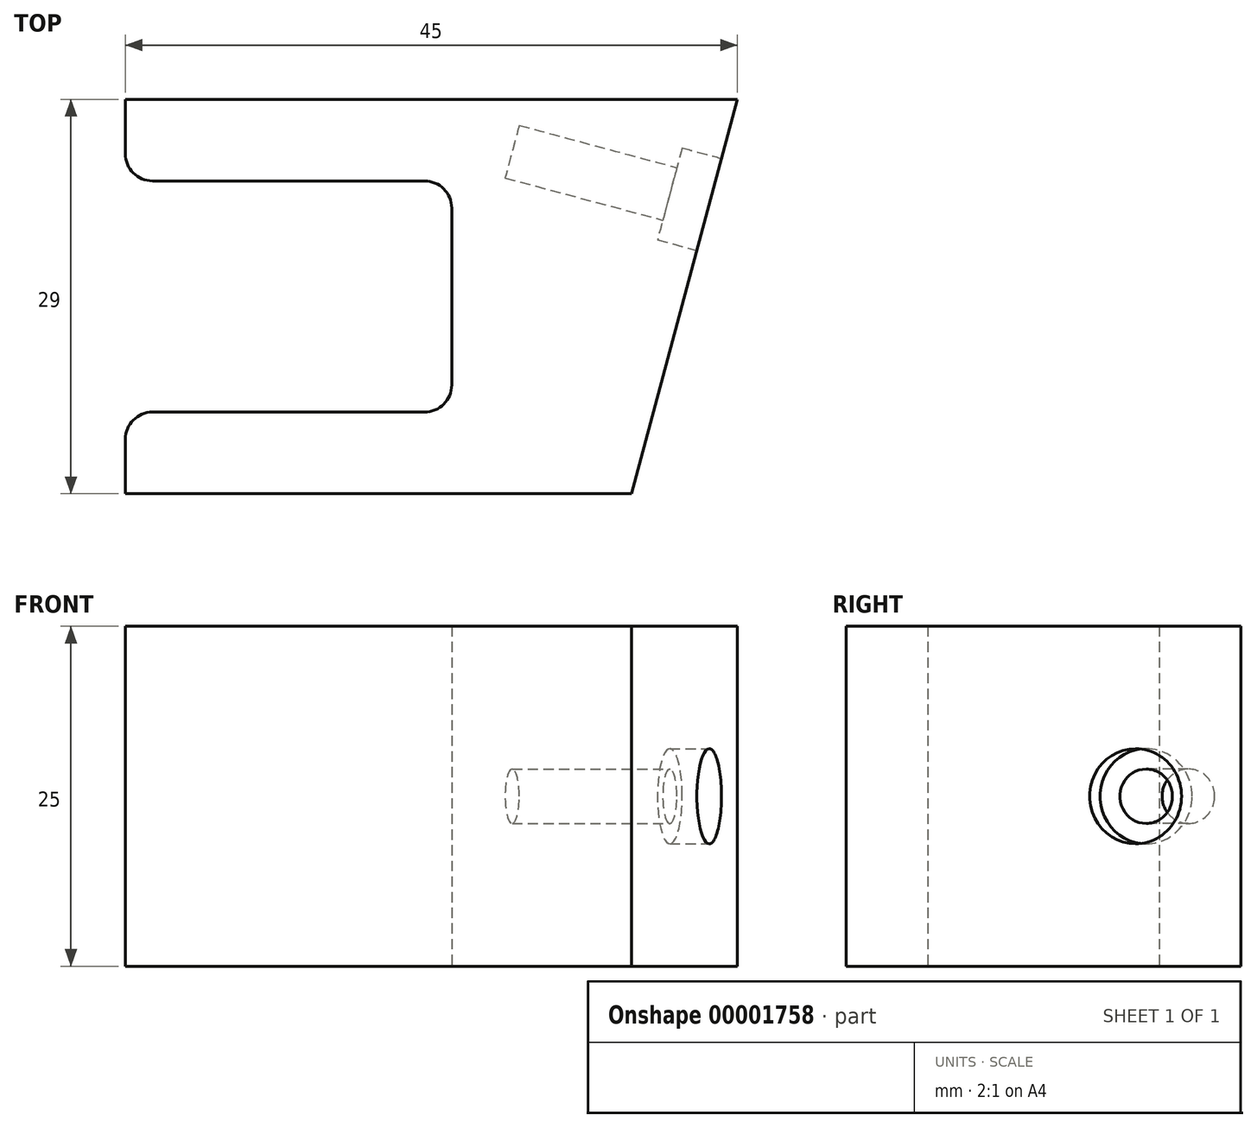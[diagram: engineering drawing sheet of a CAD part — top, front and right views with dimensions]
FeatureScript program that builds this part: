
annotation { "Feature Type Name" : "Feature", "Feature Type Description" : "" }
export const myFeature = defineFeature(function(context is Context, id is Id, definition is map)
    precondition{}
    {
        {
            var Q0;
            Q0=qCreatedBy(makeId("Top.planeOp"),FACE);
            var sketch = newSketch(context, id + "F0", { "sketchPlane" : qUnion([Q0])});
            skLineSegment(sketch, "E0.bottom", {"start": v(0, 29) * mm, "end": v(45, 29) * mm});
            skLineSegment(sketch, "E0.top", {"start": v(0, 0) * mm, "end": v(37.23, 0) * mm});
            skLineSegment(sketch, "E0.left", {"start": v(0, 29) * mm, "end": v(0, 23) * mm});
            skLineSegment(sketch, "E1", {"start": v(0, 0) * mm, "end": v(0, 6) * mm});
            skLineSegment(sketch, "E2", {"start": v(0, 6) * mm, "end": v(24, 6) * mm});
            skLineSegment(sketch, "E3", {"start": v(24, 6) * mm, "end": v(24, 23) * mm});
            skLineSegment(sketch, "E4", {"start": v(24, 23) * mm, "end": v(0, 23) * mm});
            skLineSegment(sketch, "E5", {"start": v(0, 23) * mm, "end": v(0, 29) * mm});
            skLineSegment(sketch, "E6.trimOffspring", {"start": v(0, 6) * mm, "end": v(0, 0) * mm});
            skLineSegment(sketch, "E7", {"start": v(45, 29) * mm, "end": v(37.23, 0) * mm});
            skPoint(sketch, "E8.orphan", {"position": v(45, 0) * mm});
            skSolve(sketch);
        }
        {
            var Q0;
            Q0=makeQuery(id+"F0.imprint","IMPRINT",FACE,{"disambiguationData":[TD([[makeQuery(id+"F0.imprint","IMPRINT",EDGE,{"derivedFrom":sQuery(id+"F0.wireOp",EDGE,"E0.bottom")}),-1.0]])]});
            extrude(context, id + "F1", {"entities" : qUnion([Q0]), "depth" : 25 * mm});
        }
        {
            var Q0;
            Q0=makeQuery(id+"F1.opExtrude","SWEPT_FACE",FACE,{"disambiguationData":[OSD([sQuery(id+"F0.wireOp",EDGE,"E7")])]});
            var sketch = newSketch(context, id + "F2", { "sketchPlane" : qUnion([Q0])});
            skCircle(sketch, "E9", {"center": v(31.66, 12.5) * mm, "radius": 2 * mm});
            skSolve(sketch);
        }
        {
            var Q0;
            Q0=makeQuery(id+"F2.imprint","IMPRINT",FACE,{"disambiguationData":[TD([[makeQuery(id+"F2.imprint","IMPRINT",EDGE,{"derivedFrom":sQuery(id+"F2.wireOp",EDGE,"E9")}),-1.0]])]});
            var sketch = newSketch(context, id + "F3", { "sketchPlane" : qUnion([Q0])});
            skCircle(sketch, "E10", {"center": v(31.66, 12.5) * mm, "radius": 3.5 * mm});
            skSolve(sketch);
        }
        {
            var Q0;
            Q0=makeQuery(id+"F2.imprint","IMPRINT",FACE,{"disambiguationData":[TD([[makeQuery(id+"F2.imprint","IMPRINT",EDGE,{"derivedFrom":sQuery(id+"F2.wireOp",EDGE,"E9")}),1.0]])]});
            extrude(context, id + "F4", {"entities" : qUnion([Q0]), "operationType" : NewBodyOperationType.REMOVE, "oppositeDirection" : true, "depth" : 15 * mm});
        }
        {
            var Q0;
            Q0 = qSketchRegion(id + "F3", true);
            extrude(context, id + "F5", {"entities" : qUnion([Q0]), "operationType" : NewBodyOperationType.REMOVE, "oppositeDirection" : true, "depth" : 3 * mm});
        }
        {
            var Q0;
            Q0=makeQuery(id+"F1.opExtrude","SWEPT_EDGE",EDGE,{"disambiguationData":[OSD([sQuery(id+"F0.wireOp",EDGE,"E2"),sQuery(id+"F0.wireOp",EDGE,"E6.trimOffspring")])]});
            var Q1;
            Q1=makeQuery(id+"F1.opExtrude","SWEPT_EDGE",EDGE,{"disambiguationData":[OSD([sQuery(id+"F0.wireOp",EDGE,"E4"),sQuery(id+"F0.wireOp",EDGE,"E5")])]});
            fillet(context, id + "F6", {"entities" : qUnion([Q0, Q1]), "radius" : 2 * mm, "tangentPropagation" : true, "allowEdgeOverflow" : false});
        }
    });
